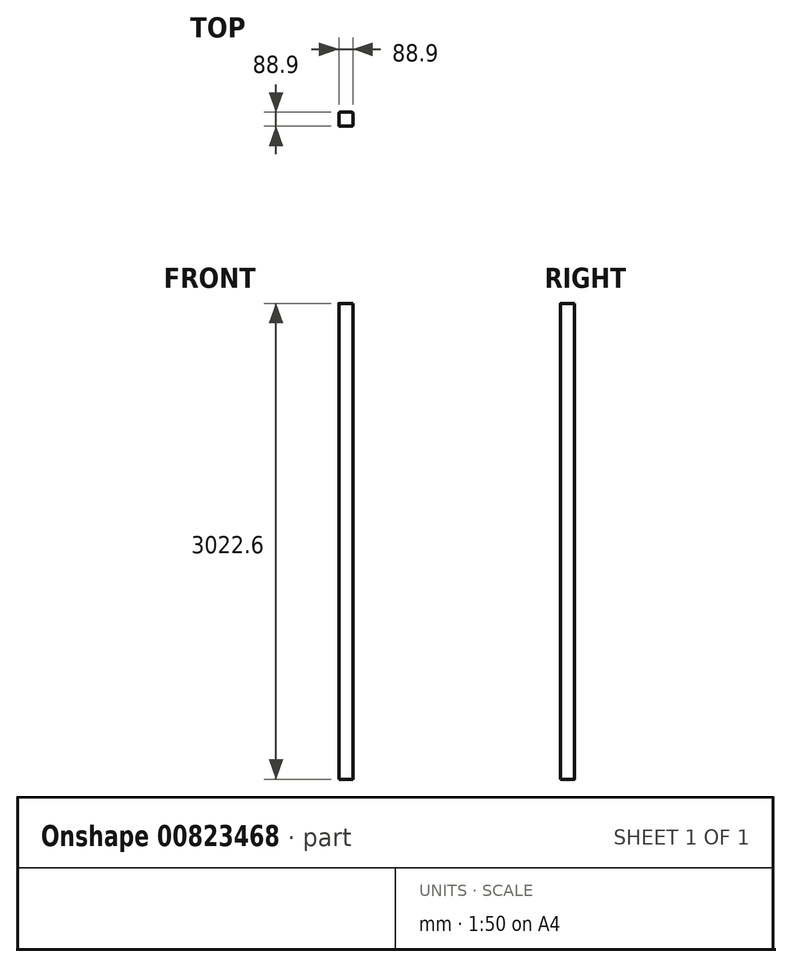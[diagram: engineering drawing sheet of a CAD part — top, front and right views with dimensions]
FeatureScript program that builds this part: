
annotation { "Feature Type Name" : "Feature", "Feature Type Description" : "" }
export const myFeature = defineFeature(function(context is Context, id is Id, definition is map)
    precondition{}
    {
        {
            var Q0;
            Q0=qCreatedBy(makeId("Top.planeOp"),FACE);
            var sketch = newSketch(context, id + "F0", { "sketchPlane" : qUnion([Q0])});
            skLineSegment(sketch, "E0.bottom", {"start": v(38.1, 44.45) * mm, "end": v(-38.1, 44.45) * mm});
            skLineSegment(sketch, "E0.top", {"start": v(38.1, -44.45) * mm, "end": v(-38.1, -44.45) * mm});
            skLineSegment(sketch, "E0.left", {"start": v(44.45, 38.1) * mm, "end": v(44.45, -38.1) * mm});
            skLineSegment(sketch, "E0.right", {"start": v(-44.45, 38.1) * mm, "end": v(-44.45, -38.1) * mm});
            skPoint(sketch, "E0.middle", {"position": v(0, 0) * mm});
            skPoint(sketch, "E1.visualSharp", {"position": v(-44.45, 44.45) * mm});
            skArc(sketch, "E1.filletArc", {"start": v(-38.1, 44.45) * mm, "mid": v(-42.6, 42.6) * mm, "end": v(-44.45, 38.1) * mm});
            skPoint(sketch, "E2.visualSharp", {"position": v(-44.45, -44.45) * mm});
            skArc(sketch, "E2.filletArc", {"start": v(-44.45, -38.1) * mm, "mid": v(-42.6, -42.6) * mm, "end": v(-38.1, -44.45) * mm});
            skPoint(sketch, "E3.visualSharp", {"position": v(44.45, -44.45) * mm});
            skArc(sketch, "E3.filletArc", {"start": v(38.1, -44.45) * mm, "mid": v(42.6, -42.6) * mm, "end": v(44.45, -38.1) * mm});
            skPoint(sketch, "E4.visualSharp", {"position": v(44.45, 44.45) * mm});
            skArc(sketch, "E4.filletArc", {"start": v(44.45, 38.1) * mm, "mid": v(42.6, 42.6) * mm, "end": v(38.1, 44.45) * mm});
            skSolve(sketch);
        }
        {
            var Q0;
            Q0 = qSketchRegion(id + "F0", true);
            extrude(context, id + "F1", {"entities" : qUnion([Q0]), "depth" : 3022.6 * mm, "offsetDistance" : 25.4 * mm});
        }
    });
